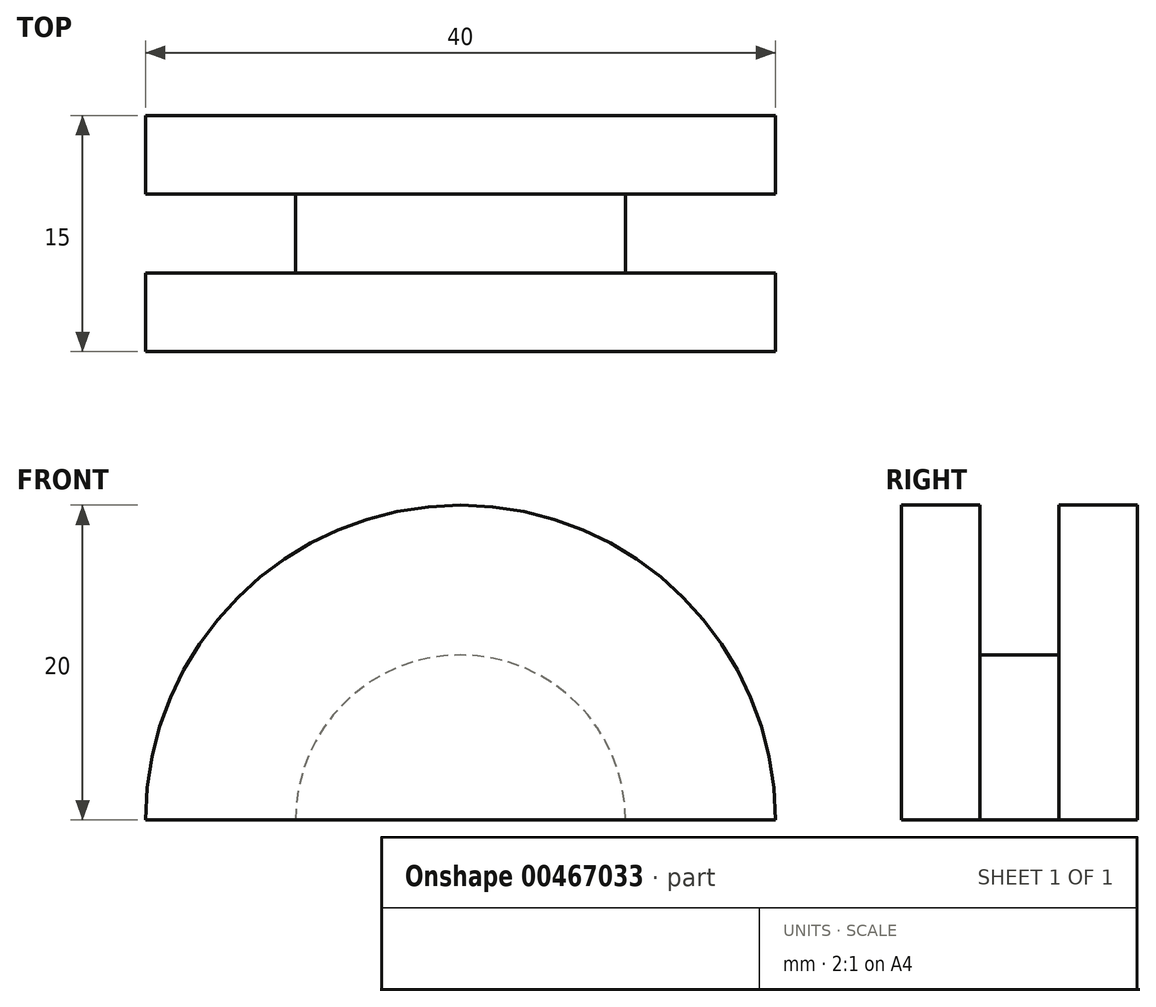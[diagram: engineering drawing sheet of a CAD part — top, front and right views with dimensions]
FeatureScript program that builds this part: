
annotation { "Feature Type Name" : "Feature", "Feature Type Description" : "" }
export const myFeature = defineFeature(function(context is Context, id is Id, definition is map)
    precondition{}
    {
        {
            var Q0;
            Q0=qCreatedBy(makeId("Front.planeOp"),FACE);
            var sketch = newSketch(context, id + "F0", { "sketchPlane" : qUnion([Q0])});
            skCircle(sketch, "E0", {"center": v(0, 0) * mm, "radius": 20 * mm});
            skSolve(sketch);
        }
        {
            var Q0;
            Q0 = qSketchRegion(id + "F0", true);
            extrude(context, id + "F1", {"entities" : qUnion([Q0]), "depth" : 5 * mm});
        }
        {
            var Q0;
            Q0=makeQuery(id+"F1.opExtrude","CAP_FACE",FACE,{"disambiguationData":[OSD([sQuery(id+"F0.wireOp",EDGE,"E0")])],"isStart":false});
            var sketch = newSketch(context, id + "F2", { "sketchPlane" : qUnion([Q0])});
            skCircle(sketch, "E1", {"center": v(0, 0) * mm, "radius": 10.48 * mm});
            skSolve(sketch);
        }
        {
            var Q0;
            Q0 = qSketchRegion(id + "F2", true);
            extrude(context, id + "F3", {"entities" : qUnion([Q0]), "operationType" : NewBodyOperationType.ADD, "depth" : 5 * mm});
        }
        {
            var Q0;
            Q0=makeQuery(id+"F3.opExtrude","CAP_FACE",FACE,{"disambiguationData":[OSD([sQuery(id+"F2.wireOp",EDGE,"E1")])],"isStart":false});
            var sketch = newSketch(context, id + "F4", { "sketchPlane" : qUnion([Q0])});
            skCircle(sketch, "E2", {"center": v(0, 0) * mm, "radius": 20 * mm});
            skSolve(sketch);
        }
        {
            var Q0;
            Q0 = qSketchRegion(id + "F4", true);
            extrude(context, id + "F5", {"entities" : qUnion([Q0]), "operationType" : NewBodyOperationType.ADD, "depth" : 5 * mm});
        }
        {
            var Q0;
            Q0=makeQuery(id+"F5.opExtrude","CAP_FACE",FACE,{"disambiguationData":[OSD([sQuery(id+"F4.wireOp",EDGE,"E2")])],"isStart":false});
            var sketch = newSketch(context, id + "F6", { "sketchPlane" : qUnion([Q0])});
            skLineSegment(sketch, "E3", {"start": v(-35.47, 0) * mm, "end": v(42.73, 0) * mm});
            skLineSegment(sketch, "E4", {"start": v(42.73, 0) * mm, "end": v(42.73, -32.4) * mm});
            skLineSegment(sketch, "E5", {"start": v(42.73, -32.4) * mm, "end": v(-28.76, -32.4) * mm});
            skLineSegment(sketch, "E6", {"start": v(-28.76, -32.4) * mm, "end": v(-35.47, 0) * mm});
            skSolve(sketch);
        }
        {
            var Q0;
            Q0 = qSketchRegion(id + "F6", true);
            extrude(context, id + "F7", {"entities" : qUnion([Q0]), "operationType" : NewBodyOperationType.REMOVE, "oppositeDirection" : true, "depth" : 25 * mm});
        }
    });
